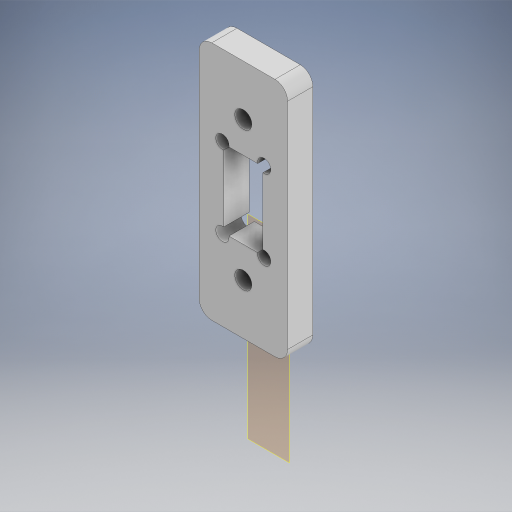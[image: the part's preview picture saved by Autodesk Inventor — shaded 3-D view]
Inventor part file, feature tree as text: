
AUTODESK INVENTOR PART (.ipt)
format: ipt  version: 2024 (Build 280153000, 153)  size: 340,992 bytes
history: native  units: mm
features: other x5, sketch x3, extrude x2, projected_geometry x2, fillet x1, hole x1, reference x1
ambient origin geometry x8: Origin, YZ Plane, XZ Plane, XY Plane, X Axis, Y Axis, Z Axis, Center Point
bodies: Body1 (feature_tree)
feature tree (15):
  other  "솔리드1"
  other  "작업 평면1"
  extrude  "돌출1"  Depth=0.3mm
  fillet  "모깎기1"  Radius=2.1mm
  extrude  "돌출2"  Depth=2.1mm
  hole  "구멍1"  [1 undecoded]
  sketch  "스케치1"
  reference  "참조1"
  sketch  "스케치2"
  projected_geometry  "투영된 루프1"
  sketch  "스케치3"
  projected_geometry  "투영된 루프2"
  other  "<userpath>\Desktop\ZIG\조립품1.iam"
  other  "조립품1.iam"
  other  "body_toptop:1"
note: 1 required parameter value undecoded (feature->parameter linkage not recoverable at this tier; creation-order binding heuristic only, values carry confidence <= 0.55)
